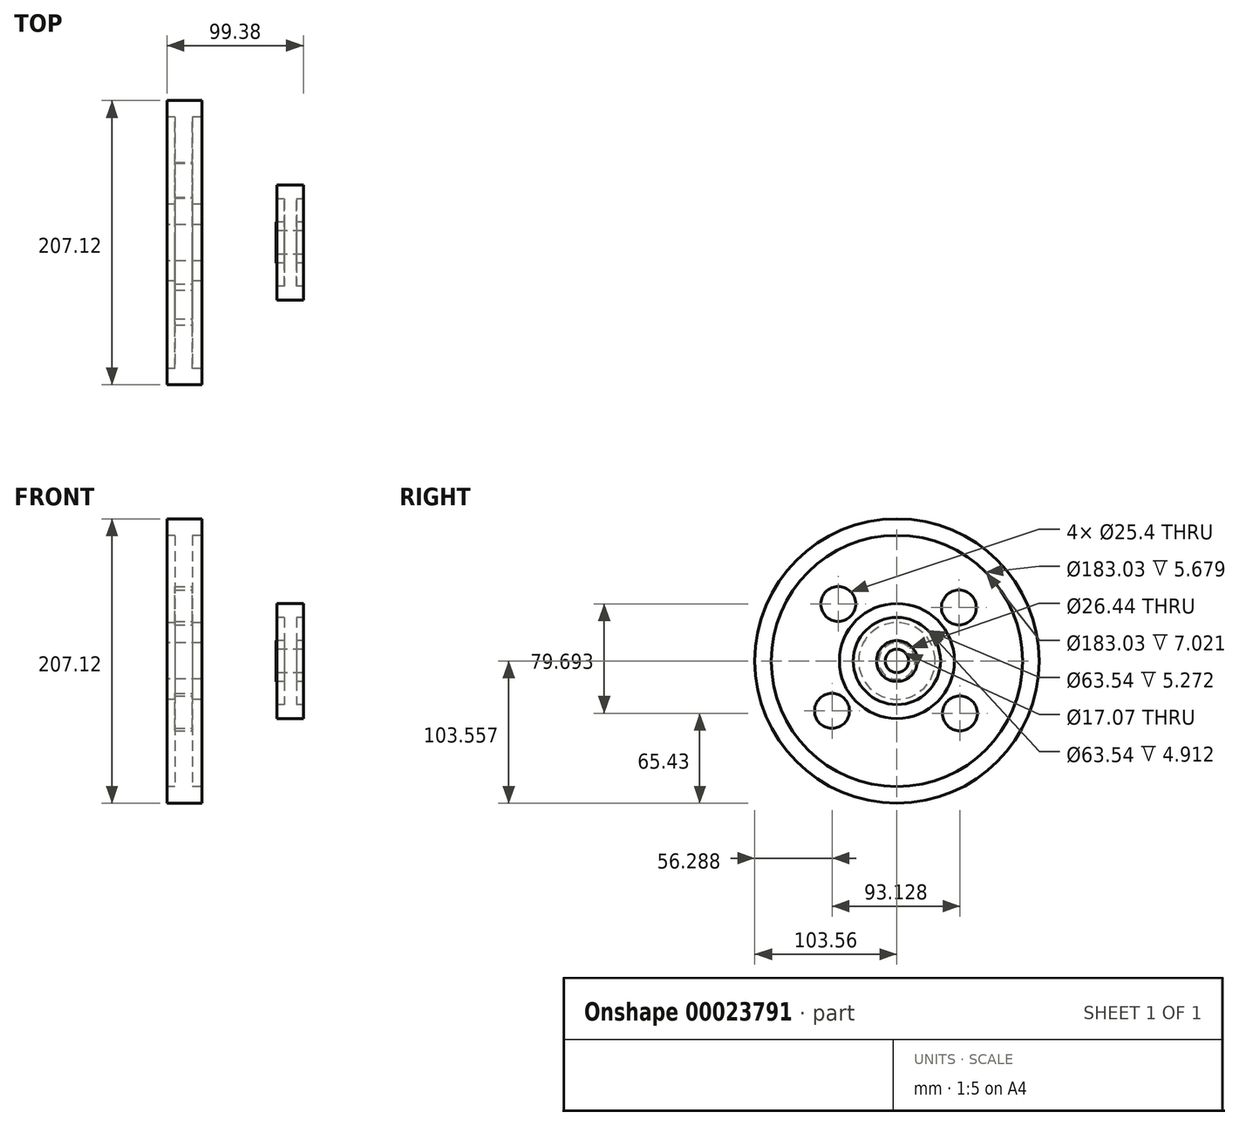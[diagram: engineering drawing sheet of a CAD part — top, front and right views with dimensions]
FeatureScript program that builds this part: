
annotation { "Feature Type Name" : "Feature", "Feature Type Description" : "" }
export const myFeature = defineFeature(function(context is Context, id is Id, definition is map)
    precondition{}
    {
        {
            var Q0;
            Q0=qCreatedBy(makeId("Front.planeOp"),FACE);
            var sketch = newSketch(context, id + "F0", { "sketchPlane" : qUnion([Q0])});
            skLineSegment(sketch, "E0.bottom", {"start": v(-86.98, 21.58) * mm, "end": v(-61.58, 21.58) * mm});
            skLineSegment(sketch, "E0.top", {"start": v(-86.98, 9.53) * mm, "end": v(-61.58, 9.53) * mm});
            skLineSegment(sketch, "E0.left", {"start": v(-86.98, 21.58) * mm, "end": v(-86.98, 9.53) * mm});
            skLineSegment(sketch, "E0.right", {"start": v(-61.58, 21.58) * mm, "end": v(-61.58, 9.53) * mm});
            skLineSegment(sketch, "E1.bottom", {"start": v(-81.3, 9.53) * mm, "end": v(-68.6, 9.53) * mm});
            skLineSegment(sketch, "E1.top", {"start": v(-81.3, -54.1) * mm, "end": v(-68.6, -54.1) * mm});
            skLineSegment(sketch, "E1.left", {"start": v(-81.3, 9.53) * mm, "end": v(-81.3, -54.1) * mm});
            skLineSegment(sketch, "E1.right", {"start": v(-68.6, 9.53) * mm, "end": v(-68.6, -54.1) * mm});
            skLineSegment(sketch, "E2.bottom", {"start": v(-86.98, -54.1) * mm, "end": v(-61.58, -54.1) * mm});
            skLineSegment(sketch, "E2.top", {"start": v(-86.98, -68.76) * mm, "end": v(-61.58, -68.76) * mm});
            skLineSegment(sketch, "E2.left", {"start": v(-86.98, -54.1) * mm, "end": v(-86.98, -68.76) * mm});
            skLineSegment(sketch, "E2.right", {"start": v(-61.58, -54.1) * mm, "end": v(-61.58, -68.76) * mm});
            skLineSegment(sketch, "E3", {"start": v(-103.05, 37.46) * mm, "end": v(-103.05, -55.13) * mm, "construction": true});
            skLineSegment(sketch, "E4", {"start": v(-126.62, -81.98) * mm, "end": v(-7.4, -81.98) * mm, "construction": true});
            skLineSegment(sketch, "E5", {"start": v(61.22, -70.27) * mm, "end": v(-7.2, -70.27) * mm, "construction": true});
            skLineSegment(sketch, "E6.bottom", {"start": v(-6.89, -50.21) * mm, "end": v(12.4, -50.21) * mm});
            skLineSegment(sketch, "E6.top", {"start": v(-6.89, -40.1) * mm, "end": v(12.4, -40.1) * mm});
            skLineSegment(sketch, "E6.left", {"start": v(-6.89, -40.1) * mm, "end": v(-6.89, -50.21) * mm});
            skLineSegment(sketch, "E6.right", {"start": v(12.4, -40.1) * mm, "end": v(12.4, -50.21) * mm});
            skLineSegment(sketch, "E7.bottom", {"start": v(-1.62, -50.21) * mm, "end": v(7.49, -50.21) * mm});
            skLineSegment(sketch, "E7.top", {"start": v(-1.62, -73.45) * mm, "end": v(7.49, -73.45) * mm});
            skLineSegment(sketch, "E7.left", {"start": v(-1.62, -73.45) * mm, "end": v(-1.62, -50.21) * mm});
            skLineSegment(sketch, "E7.right", {"start": v(7.49, -73.45) * mm, "end": v(7.49, -50.21) * mm});
            skLineSegment(sketch, "E8.bottom", {"start": v(-7.49, -73.45) * mm, "end": v(12.4, -73.45) * mm});
            skLineSegment(sketch, "E8.top", {"start": v(-7.49, -67.1) * mm, "end": v(12.4, -67.1) * mm});
            skLineSegment(sketch, "E8.left", {"start": v(-7.49, -73.45) * mm, "end": v(-7.49, -67.1) * mm});
            skLineSegment(sketch, "E8.right", {"start": v(12.4, -73.45) * mm, "end": v(12.4, -67.1) * mm});
            skSolve(sketch);
        }
        {
            var Q0;
            Q0 = qSketchRegion(id + "F0", true);
            var Q1;
            Q1=sQuery(id+"F0.wireOp",EDGE,"E4");
            revolve(context, id + "F1", {"entities" : qUnion([Q0]), "axis" : qUnion([Q1]), "revolveType" : RevolveType.FULL});
        }
        {
            var Q0;
            Q0=makeQuery(id+"F1.opRevolve","SWEPT_FACE",FACE,{"disambiguationData":[OSD([sQuery(id+"F0.wireOp",EDGE,"E1.right")])]});
            var sketch = newSketch(context, id + "F2", { "sketchPlane" : qUnion([Q0])});
            skCircle(sketch, "E9", {"center": v(-47.27, -118.34) * mm, "radius": 12.7 * mm});
            skCircle(sketch, "E10", {"center": v(45.86, -120.1) * mm, "radius": 12.7 * mm});
            skCircle(sketch, "E11", {"center": v(45.17, -43.04) * mm, "radius": 12.7 * mm});
            skCircle(sketch, "E12", {"center": v(-42.76, -40.42) * mm, "radius": 12.7 * mm});
            skSolve(sketch);
        }
        {
            var Q0;
            Q0=sQuery(id+"F2.wireOp",VERTEX,"E10.center");
            var Q1;
            Q1=sQuery(id+"F2.wireOp",VERTEX,"E9.center");
            var Q2;
            Q2=sQuery(id+"F2.wireOp",VERTEX,"E11.center");
            var Q3;
            Q3=sQuery(id+"F2.wireOp",VERTEX,"E12.center");
            var Q4;
            Q4=makeQuery(id+"F1.opRevolve","SWEPT_BODY",BODY,{"disambiguationData":[OSD([sQuery(id+"F0.wireOp",EDGE,"E0.bottom"),sQuery(id+"F0.wireOp",EDGE,"E0.top"),sQuery(id+"F0.wireOp",EDGE,"E0.left"),sQuery(id+"F0.wireOp",EDGE,"E0.right"),sQuery(id+"F0.wireOp",EDGE,"E1.left"),sQuery(id+"F0.wireOp",EDGE,"E1.right"),sQuery(id+"F0.wireOp",EDGE,"E2.bottom"),sQuery(id+"F0.wireOp",EDGE,"E2.top"),sQuery(id+"F0.wireOp",EDGE,"E2.left"),sQuery(id+"F0.wireOp",EDGE,"E2.right")])]});
            hole(context, id + "F3", {"style" : HoleStyle.SIMPLE, "holeDiameter" : 25.4 * mm, "endStyle" : HoleEndStyle.THROUGH, "locations" : qUnion([Q0, Q1, Q2, Q3]), "scope" : qUnion([Q4])});
        }
    });
